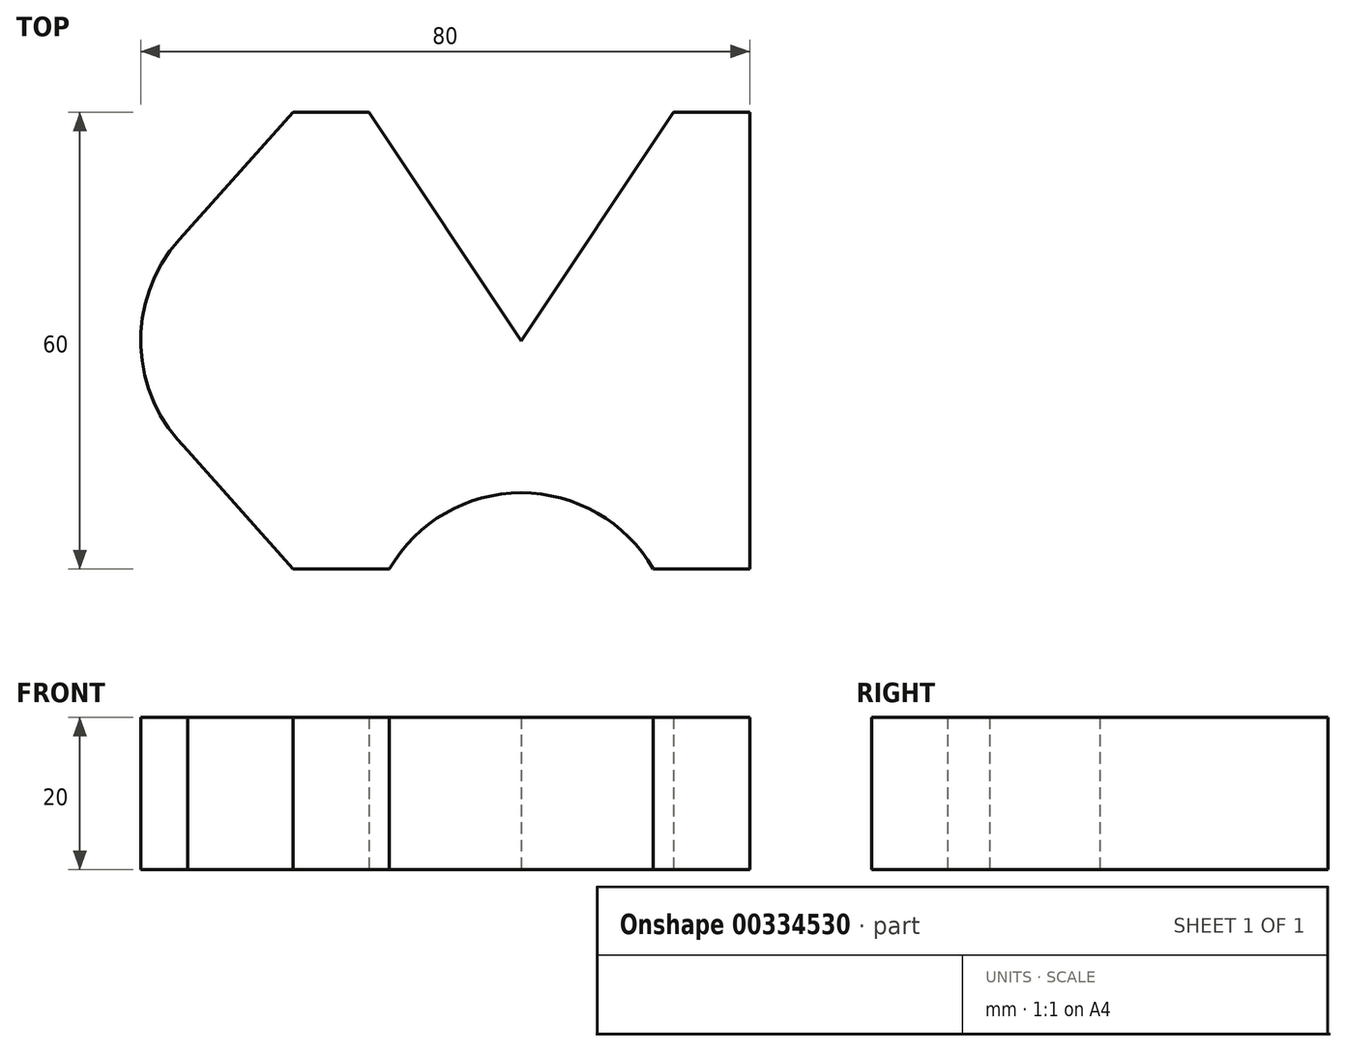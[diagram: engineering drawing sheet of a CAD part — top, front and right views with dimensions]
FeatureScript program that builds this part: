
annotation { "Feature Type Name" : "Feature", "Feature Type Description" : "" }
export const myFeature = defineFeature(function(context is Context, id is Id, definition is map)
    precondition{}
    {
        {
            var Q0;
            Q0=qCreatedBy(makeId("Top.planeOp"),FACE);
            var sketch = newSketch(context, id + "F0", { "sketchPlane" : qUnion([Q0])});
            skCircle(sketch, "E0", {"center": v(-30, 0) * mm, "radius": 20 * mm});
            skLineSegment(sketch, "E1", {"start": v(-44.9, 13.33) * mm, "end": v(-30, 30) * mm});
            skLineSegment(sketch, "E2", {"start": v(-30, 30) * mm, "end": v(-20, 30) * mm});
            skLineSegment(sketch, "E3", {"start": v(-20, 30) * mm, "end": v(0, 0) * mm});
            skLineSegment(sketch, "E4", {"start": v(0, 0) * mm, "end": v(20, 30) * mm});
            skLineSegment(sketch, "E5", {"start": v(20, 30) * mm, "end": v(30, 30) * mm});
            skLineSegment(sketch, "E6", {"start": v(30, 30) * mm, "end": v(30, -30) * mm});
            skLineSegment(sketch, "E7", {"start": v(30, -30) * mm, "end": v(0, -30) * mm});
            skLineSegment(sketch, "E8", {"start": v(-30, -30) * mm, "end": v(-43.8, -14.47) * mm});
            skLineSegment(sketch, "E9", {"start": v(-30, -30) * mm, "end": v(0, -30) * mm});
            skCircle(sketch, "E10", {"center": v(0, -40) * mm, "radius": 20 * mm});
            skSolve(sketch);
        }
        {
            var Q0;
            {var subQ7=sQuery(id+"F0.wireOp",EDGE,"E1");Q0=makeQuery(id+"F0.imprint","IMPRINT",FACE,{"disambiguationData":[TD([[makeQuery(id+"F0.imprint","IMPRINT",EDGE,{"derivedFrom":subQ7}),-1.0]])]});}
            var Q1;
            {var subQ0=sQuery(id+"F0.wireOp",EDGE,"E0");var subQ1=makeQuery(id+"F0.imprint","INTERSECT",VERTEX,{"derivedFrom":[subQ0,sQuery(id+"F0.wireOp",EDGE,"E1")]});Q1=makeQuery(id+"F0.imprint","IMPRINT",FACE,{"disambiguationData":[TD([[makeQuery(id+"F0.imprint","IMPRINT",EDGE,{"disambiguationData":[TD([[subQ1,-1.0]])],"derivedFrom":subQ0}),1.0]])]});}
            extrude(context, id + "F1", {"entities" : qUnion([Q0, Q1]), "depth" : 20 * mm});
        }
    });
